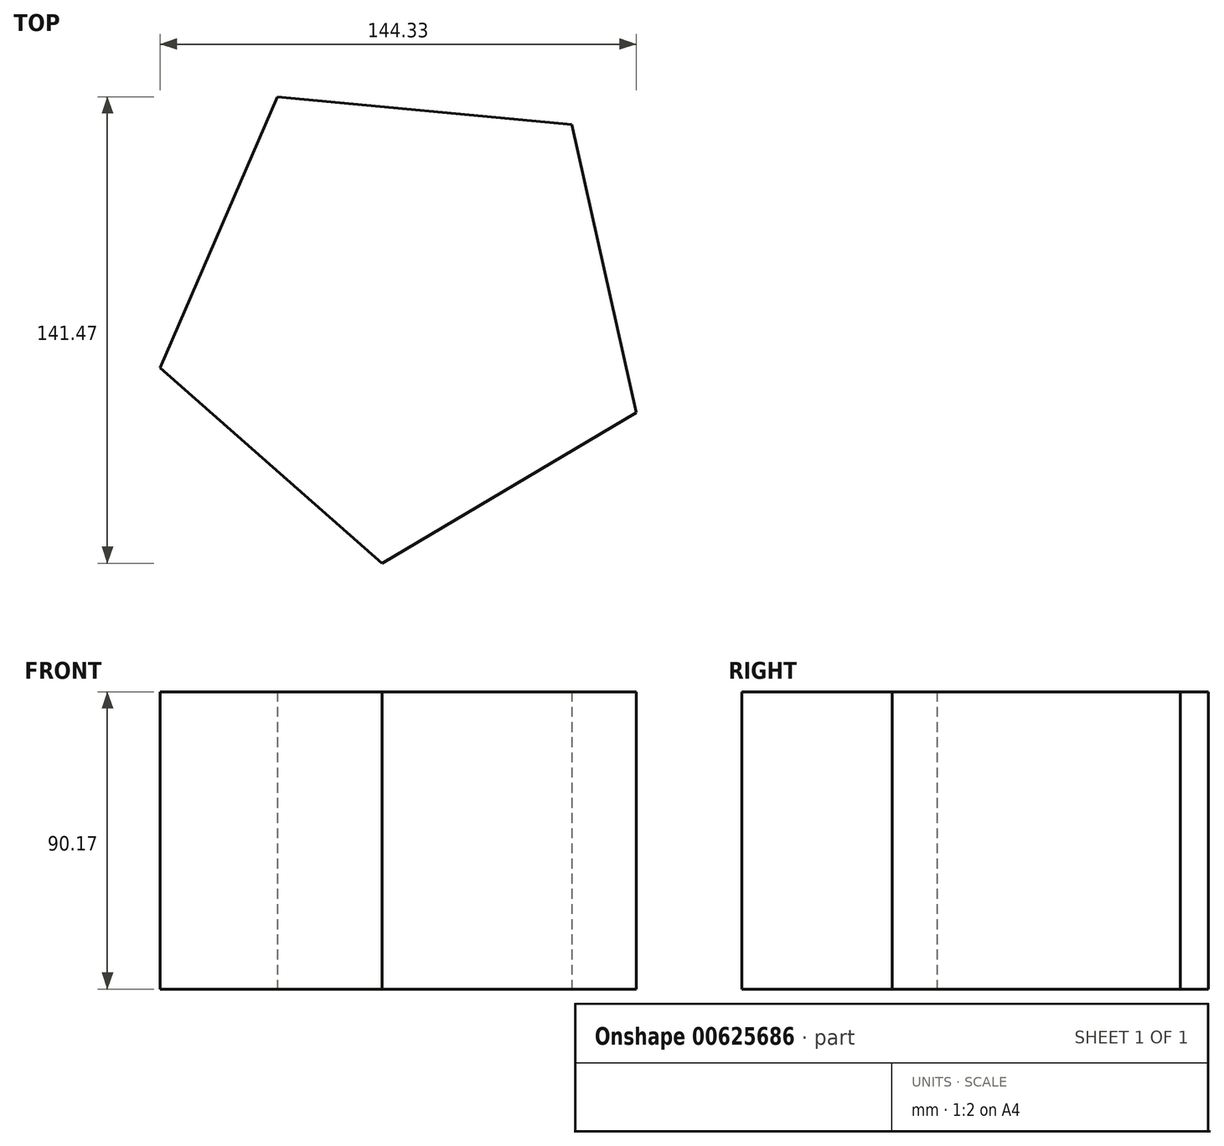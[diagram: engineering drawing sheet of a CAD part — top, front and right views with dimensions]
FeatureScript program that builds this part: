
annotation { "Feature Type Name" : "Feature", "Feature Type Description" : "" }
export const myFeature = defineFeature(function(context is Context, id is Id, definition is map)
    precondition{}
    {
        {
            var Q0;
            Q0=qCreatedBy(makeId("Top.planeOp"),FACE);
            var sketch = newSketch(context, id + "F0", { "sketchPlane" : qUnion([Q0])});
            skCircle(sketch, "E0.cCircle", {"center": v(0, 0) * mm, "radius": 61.66 * mm, "construction": true});
            skLineSegment(sketch, "E0.0", {"start": v(-74.37, -16.65) * mm, "end": v(-38.82, 65.59) * mm});
            skLineSegment(sketch, "E0.1", {"start": v(-38.82, 65.59) * mm, "end": v(50.38, 57.19) * mm});
            skLineSegment(sketch, "E0.2", {"start": v(50.38, 57.19) * mm, "end": v(69.96, -30.24) * mm});
            skLineSegment(sketch, "E0.3", {"start": v(69.96, -30.24) * mm, "end": v(-7.14, -75.88) * mm});
            skLineSegment(sketch, "E0.4", {"start": v(-7.14, -75.88) * mm, "end": v(-74.37, -16.65) * mm});
            skPoint(sketch, "E0.0.midPoint", {"position": v(-56.6, 24.47) * mm});
            skSolve(sketch);
        }
        {
            var Q0;
            Q0=makeQuery(id+"F0.imprint","IMPRINT",FACE,{"disambiguationData":[TD([[makeQuery(id+"F0.imprint","IMPRINT",EDGE,{"derivedFrom":sQuery(id+"F0.wireOp",EDGE,"E0.0")}),-1.0]])]});
            extrude(context, id + "F1", {"entities" : qUnion([Q0]), "depth" : 90.17 * mm, "offsetDistance" : 25.4 * mm});
        }
    });
